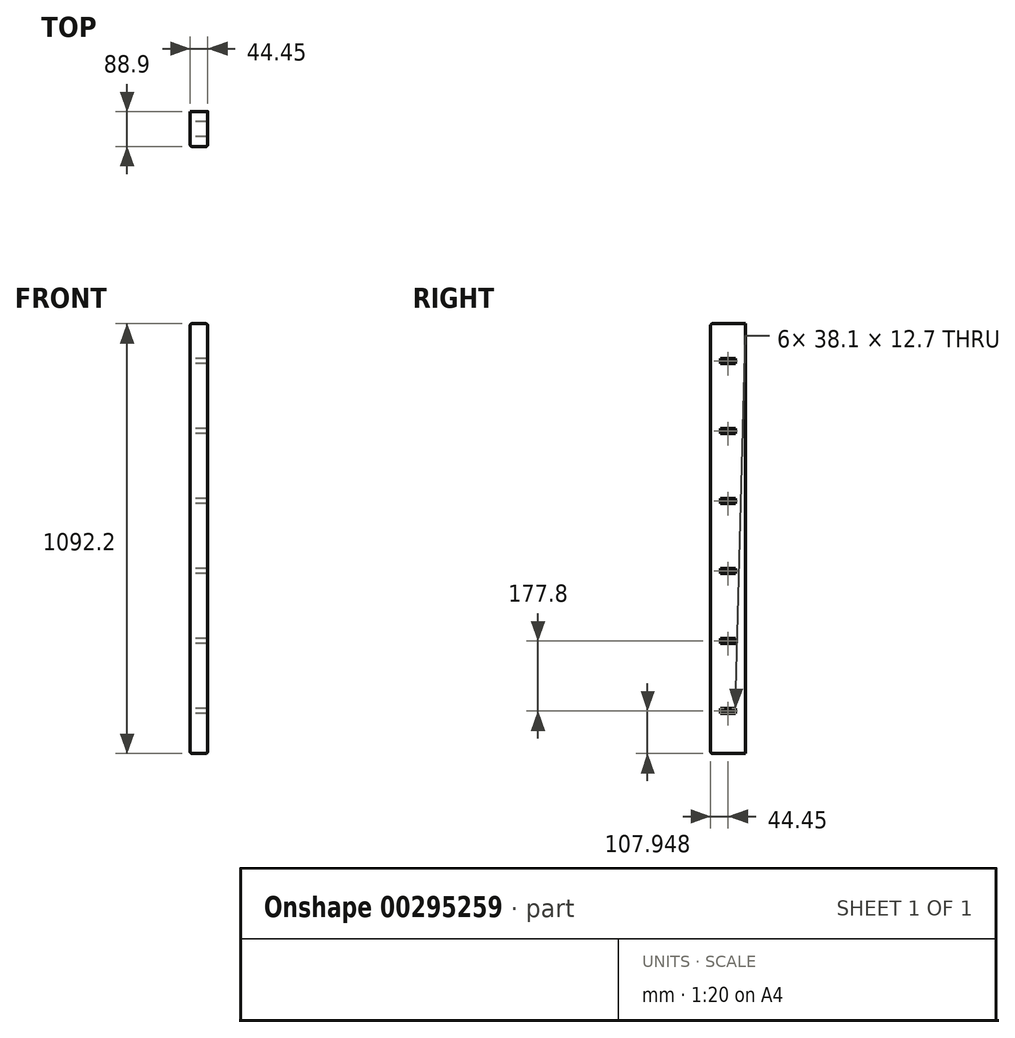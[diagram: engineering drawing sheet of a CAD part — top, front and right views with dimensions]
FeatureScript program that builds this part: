
annotation { "Feature Type Name" : "Feature", "Feature Type Description" : "" }
export const myFeature = defineFeature(function(context is Context, id is Id, definition is map)
    precondition{}
    {
        {
            var Q0;
            Q0=qCreatedBy(makeId("Front.planeOp"),FACE);
            var sketch = newSketch(context, id + "F0", { "sketchPlane" : qUnion([Q0])});
            skLineSegment(sketch, "E0.bottom", {"start": v(-44.45, 762.67) * mm, "end": v(0, 762.67) * mm});
            skLineSegment(sketch, "E0.top", {"start": v(-44.45, -329.53) * mm, "end": v(0, -329.53) * mm});
            skLineSegment(sketch, "E0.left", {"start": v(-44.45, 762.67) * mm, "end": v(-44.45, -329.53) * mm});
            skLineSegment(sketch, "E0.right", {"start": v(0, 762.67) * mm, "end": v(0, -329.53) * mm});
            skSolve(sketch);
        }
        {
            var Q0;
            Q0=makeQuery(id+"F0.imprint","IMPRINT",FACE,{"disambiguationData":[TD([[makeQuery(id+"F0.imprint","IMPRINT",EDGE,{"derivedFrom":sQuery(id+"F0.wireOp",EDGE,"E0.bottom")}),-1.0]])]});
            extrude(context, id + "F1", {"entities" : qUnion([Q0]), "depth" : 88.9 * mm});
        }
        {
            var Q0;
            Q0=makeQuery(id+"F1.opExtrude","SWEPT_FACE",FACE,{"disambiguationData":[OSD([sQuery(id+"F0.wireOp",EDGE,"E0.left")])]});
            var sketch = newSketch(context, id + "F2", { "sketchPlane" : qUnion([Q0])});
            skLineSegment(sketch, "E1.bottom", {"start": v(63.5, 673.77) * mm, "end": v(25.4, 673.77) * mm});
            skLineSegment(sketch, "E1.top", {"start": v(63.5, 661.07) * mm, "end": v(25.4, 661.07) * mm});
            skLineSegment(sketch, "E1.left", {"start": v(63.5, 673.77) * mm, "end": v(63.5, 661.07) * mm});
            skLineSegment(sketch, "E1.right", {"start": v(25.4, 673.77) * mm, "end": v(25.4, 661.07) * mm});
            skLineSegment(sketch, "E2.1.0.0", {"start": v(63.5, 483.27) * mm, "end": v(25.4, 483.27) * mm});
            skLineSegment(sketch, "E2.1.0.1", {"start": v(63.5, 495.97) * mm, "end": v(63.5, 483.27) * mm});
            skLineSegment(sketch, "E2.1.0.2", {"start": v(63.5, 495.97) * mm, "end": v(25.4, 495.97) * mm});
            skLineSegment(sketch, "E2.1.0.3", {"start": v(25.4, 495.97) * mm, "end": v(25.4, 483.27) * mm});
            skLineSegment(sketch, "E2.2.0.0", {"start": v(63.5, 305.47) * mm, "end": v(25.4, 305.47) * mm});
            skLineSegment(sketch, "E2.2.0.1", {"start": v(63.5, 318.17) * mm, "end": v(63.5, 305.47) * mm});
            skLineSegment(sketch, "E2.2.0.2", {"start": v(63.5, 318.17) * mm, "end": v(25.4, 318.17) * mm});
            skLineSegment(sketch, "E2.2.0.3", {"start": v(25.4, 318.17) * mm, "end": v(25.4, 305.47) * mm});
            skLineSegment(sketch, "E2.3.0.0", {"start": v(63.5, 127.67) * mm, "end": v(25.4, 127.67) * mm});
            skLineSegment(sketch, "E2.3.0.1", {"start": v(63.5, 140.37) * mm, "end": v(63.5, 127.67) * mm});
            skLineSegment(sketch, "E2.3.0.2", {"start": v(63.5, 140.37) * mm, "end": v(25.4, 140.37) * mm});
            skLineSegment(sketch, "E2.3.0.3", {"start": v(25.4, 140.37) * mm, "end": v(25.4, 127.67) * mm});
            skLineSegment(sketch, "E2.4.0.0", {"start": v(63.5, -50.13) * mm, "end": v(25.4, -50.13) * mm});
            skLineSegment(sketch, "E2.4.0.1", {"start": v(63.5, -37.43) * mm, "end": v(63.5, -50.13) * mm});
            skLineSegment(sketch, "E2.4.0.2", {"start": v(63.5, -37.43) * mm, "end": v(25.4, -37.43) * mm});
            skLineSegment(sketch, "E2.4.0.3", {"start": v(25.4, -37.43) * mm, "end": v(25.4, -50.13) * mm});
            skLineSegment(sketch, "E2.direction1", {"start": v(25.4, 661.07) * mm, "end": v(25.4, 483.27) * mm, "construction": true});
            skLineSegment(sketch, "E3.0.5.0", {"start": v(63.5, -227.93) * mm, "end": v(25.4, -227.93) * mm});
            skLineSegment(sketch, "E3.3.5.0", {"start": v(63.5, -215.23) * mm, "end": v(63.5, -227.93) * mm});
            skLineSegment(sketch, "E3.6.5.0", {"start": v(63.5, -215.23) * mm, "end": v(25.4, -215.23) * mm});
            skLineSegment(sketch, "E3.9.5.0", {"start": v(25.4, -215.23) * mm, "end": v(25.4, -227.93) * mm});
            skSolve(sketch);
        }
        {
            var Q0;
            Q0=makeQuery(id+"F2.imprint","IMPRINT",FACE,{"disambiguationData":[TD([[makeQuery(id+"F2.imprint","IMPRINT",EDGE,{"derivedFrom":sQuery(id+"F2.wireOp",EDGE,"E1.bottom")}),1.0]])]});
            var Q1;
            Q1=makeQuery(id+"F2.imprint","IMPRINT",FACE,{"disambiguationData":[TD([[makeQuery(id+"F2.imprint","IMPRINT",EDGE,{"derivedFrom":sQuery(id+"F2.wireOp",EDGE,"E2.4.0.0")}),-1.0]])]});
            var Q2;
            Q2=makeQuery(id+"F2.imprint","IMPRINT",FACE,{"disambiguationData":[TD([[makeQuery(id+"F2.imprint","IMPRINT",EDGE,{"derivedFrom":sQuery(id+"F2.wireOp",EDGE,"E2.3.0.0")}),-1.0]])]});
            var Q3;
            Q3=makeQuery(id+"F2.imprint","IMPRINT",FACE,{"disambiguationData":[TD([[makeQuery(id+"F2.imprint","IMPRINT",EDGE,{"derivedFrom":sQuery(id+"F2.wireOp",EDGE,"E2.2.0.0")}),-1.0]])]});
            var Q4;
            Q4=makeQuery(id+"F2.imprint","IMPRINT",FACE,{"disambiguationData":[TD([[makeQuery(id+"F2.imprint","IMPRINT",EDGE,{"derivedFrom":sQuery(id+"F2.wireOp",EDGE,"E3.0.5.0")}),-1.0]])]});
            var Q5;
            Q5=makeQuery(id+"F2.imprint","IMPRINT",FACE,{"disambiguationData":[TD([[makeQuery(id+"F2.imprint","IMPRINT",EDGE,{"derivedFrom":sQuery(id+"F2.wireOp",EDGE,"E2.1.0.0")}),-1.0]])]});
            extrude(context, id + "F3", {"entities" : qUnion([Q0, Q1, Q2, Q3, Q4, Q5]), "operationType" : NewBodyOperationType.REMOVE, "endBound" : BoundingType.THROUGH_ALL, "oppositeDirection" : true, "depth" : 25.4 * mm});
        }
        {
            var Q0;
            Q0=makeQuery(id+"F1.opExtrude","CAP_EDGE",EDGE,{"disambiguationData":[OSD([sQuery(id+"F0.wireOp",EDGE,"E0.left")])],"isStart":false});
            var Q1;
            Q1=makeQuery(id+"F1.opExtrude","CAP_EDGE",EDGE,{"disambiguationData":[OSD([sQuery(id+"F0.wireOp",EDGE,"E0.right")])],"isStart":false});
            var Q2;
            Q2=makeQuery(id+"F1.opExtrude","CAP_EDGE",EDGE,{"disambiguationData":[OSD([sQuery(id+"F0.wireOp",EDGE,"E0.bottom")])],"isStart":false});
            var Q3;
            Q3=makeQuery(id+"F1.opExtrude","SWEPT_EDGE",EDGE,{"disambiguationData":[OSD([sQuery(id+"F0.wireOp",EDGE,"E0.bottom"),sQuery(id+"F0.wireOp",EDGE,"E0.right")])]});
            var Q4;
            Q4=makeQuery(id+"F1.opExtrude","SWEPT_EDGE",EDGE,{"disambiguationData":[OSD([sQuery(id+"F0.wireOp",EDGE,"E0.bottom"),sQuery(id+"F0.wireOp",EDGE,"E0.left")])]});
            var Q5;
            Q5=makeQuery(id+"F1.opExtrude","CAP_EDGE",EDGE,{"disambiguationData":[OSD([sQuery(id+"F0.wireOp",EDGE,"E0.top")])],"isStart":false});
            var Q6;
            Q6=makeQuery(id+"F1.opExtrude","SWEPT_EDGE",EDGE,{"disambiguationData":[OSD([sQuery(id+"F0.wireOp",EDGE,"E0.top"),sQuery(id+"F0.wireOp",EDGE,"E0.right")])]});
            var Q7;
            Q7=makeQuery(id+"F1.opExtrude","SWEPT_EDGE",EDGE,{"disambiguationData":[OSD([sQuery(id+"F0.wireOp",EDGE,"E0.top"),sQuery(id+"F0.wireOp",EDGE,"E0.left")])]});
            fillet(context, id + "F4", {"entities" : qUnion([Q0, Q1, Q2, Q3, Q4, Q5, Q6, Q7]), "radius" : 5.08 * mm, "tangentPropagation" : true, "allowEdgeOverflow" : false});
        }
    });
